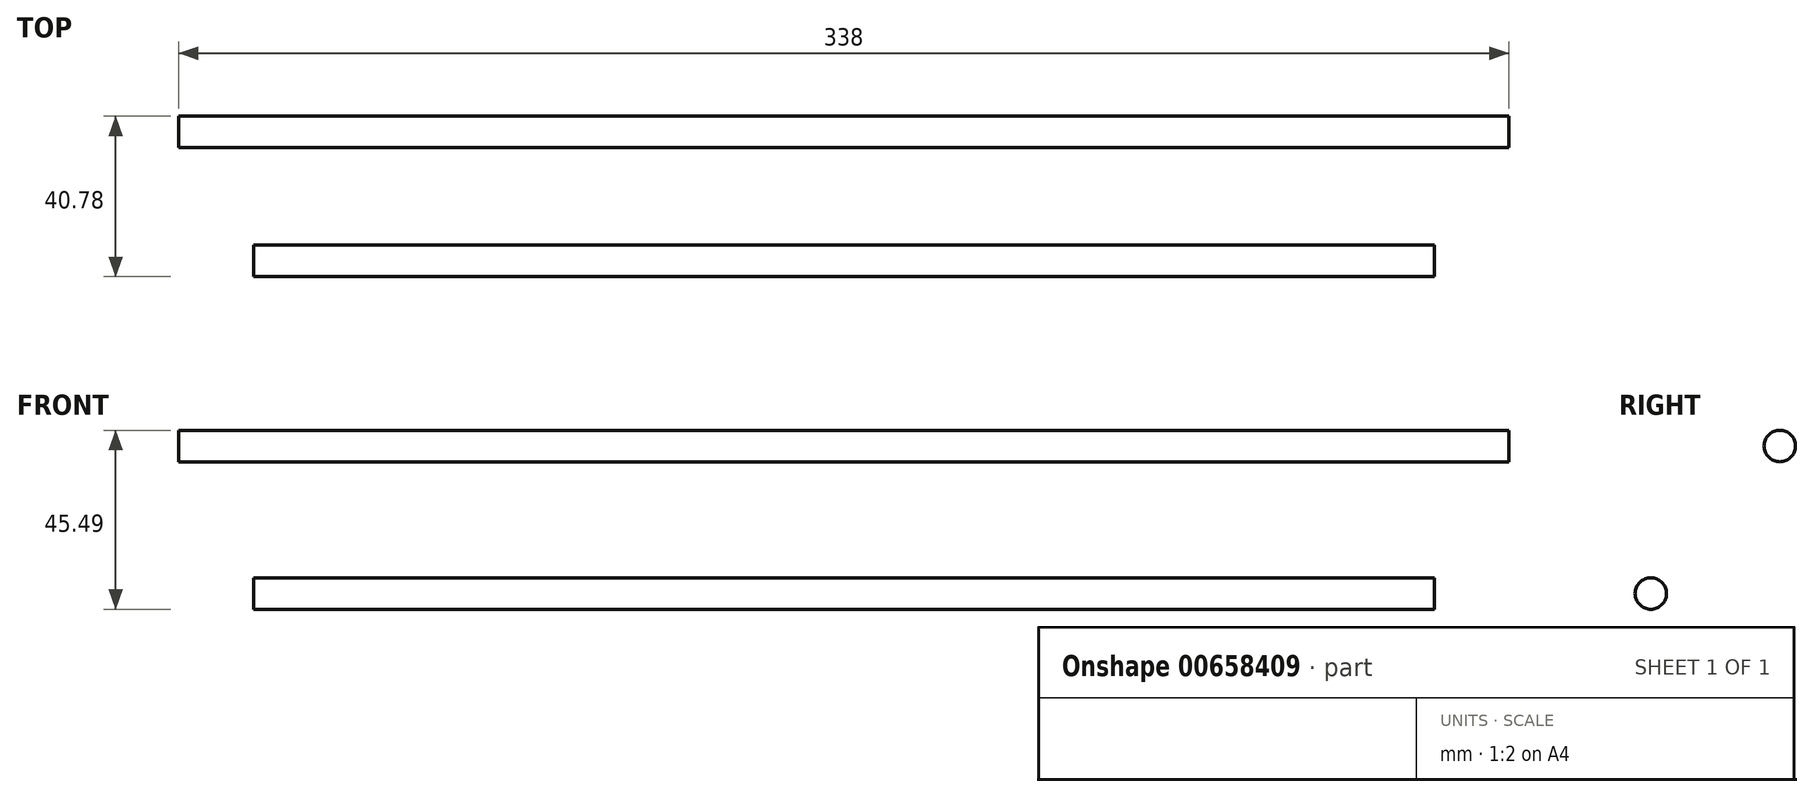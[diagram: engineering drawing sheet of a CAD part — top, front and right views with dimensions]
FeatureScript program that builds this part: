
annotation { "Feature Type Name" : "Feature", "Feature Type Description" : "" }
export const myFeature = defineFeature(function(context is Context, id is Id, definition is map)
    precondition{}
    {
        {
            assignVariable(context, id + "F0", {"name" : "xrod", "anyValue" : 300});
        }
        {
            var Q0;
            Q0=qCreatedBy(makeId("Right.planeOp"),FACE);
            var sketch = newSketch(context, id + "F1", { "sketchPlane" : qUnion([Q0])});
            skCircle(sketch, "E0", {"center": v(0, 0) * mm, "radius": 4 * mm});
            skSolve(sketch);
        }
        {
            var Q0;
            Q0=makeQuery(id+"F1.imprint","IMPRINT",FACE,{"disambiguationData":[TD([[makeQuery(id+"F1.imprint","IMPRINT",EDGE,{"derivedFrom":sQuery(id+"F1.wireOp",EDGE,"E0")}),1.0]])]});
            extrude(context, id + "F2", {"entities" : qUnion([Q0]), "endBound" : BoundingType.SYMMETRIC, "depth" : (getVariable(context, 'xrod')) * mm, "offsetDistance" : 25 * mm});
        }
        {
            var Q0;
            Q0=qCreatedBy(makeId("Right.planeOp"),FACE);
            var sketch = newSketch(context, id + "F3", { "sketchPlane" : qUnion([Q0])});
            skCircle(sketch, "E1", {"center": v(32.78, 37.49) * mm, "radius": 4 * mm});
            skSolve(sketch);
        }
        {
            var Q0;
            Q0=makeQuery(id+"F3.imprint","IMPRINT",FACE,{"disambiguationData":[TD([[makeQuery(id+"F3.imprint","IMPRINT",EDGE,{"derivedFrom":sQuery(id+"F3.wireOp",EDGE,"E1")}),1.0]])]});
            extrude(context, id + "F4", {"entities" : qUnion([Q0]), "endBound" : BoundingType.SYMMETRIC, "depth" : (320 + 18) * mm, "offsetDistance" : 25 * mm});
        }
    });
